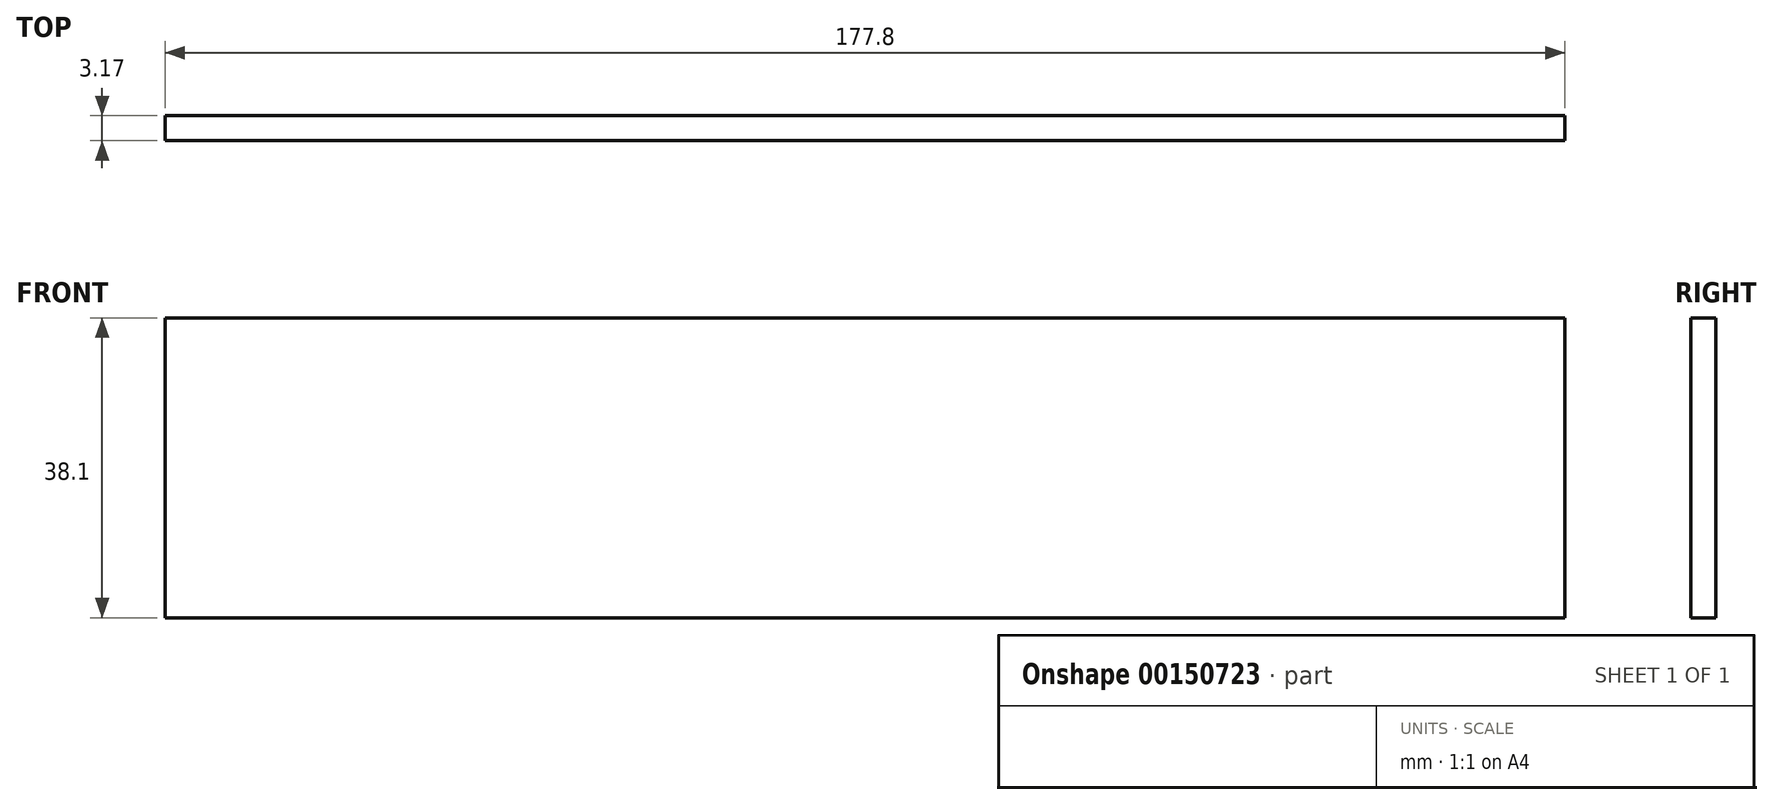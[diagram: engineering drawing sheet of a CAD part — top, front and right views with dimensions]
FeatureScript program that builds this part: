
annotation { "Feature Type Name" : "Feature", "Feature Type Description" : "" }
export const myFeature = defineFeature(function(context is Context, id is Id, definition is map)
    precondition{}
    {
        {
            var Q0;
            Q0=qCreatedBy(makeId("Front.planeOp"),FACE);
            var sketch = newSketch(context, id + "F0", { "sketchPlane" : qUnion([Q0])});
            skLineSegment(sketch, "E0.bottom", {"start": v(88.9, 19.05) * mm, "end": v(-88.9, 19.05) * mm});
            skLineSegment(sketch, "E0.top", {"start": v(88.9, -19.05) * mm, "end": v(-88.9, -19.05) * mm});
            skLineSegment(sketch, "E0.left", {"start": v(88.9, 19.05) * mm, "end": v(88.9, -19.05) * mm});
            skLineSegment(sketch, "E0.right", {"start": v(-88.9, 19.05) * mm, "end": v(-88.9, -19.05) * mm});
            skPoint(sketch, "E0.middle", {"position": v(0, 0) * mm});
            skSolve(sketch);
        }
        {
            var Q0;
            Q0 = qSketchRegion(id + "F0", true);
            extrude(context, id + "F1", {"entities" : qUnion([Q0]), "depth" : 3.17 * mm});
        }
    });
